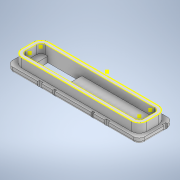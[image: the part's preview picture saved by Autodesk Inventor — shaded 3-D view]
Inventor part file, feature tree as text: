
AUTODESK INVENTOR PART (.ipt)
format: ipt  version: 2022 (Build 260153000, 153)  size: 633,344 bytes
history: native  units: in
note: dims shown in document units (in); Inventor stores cm internally (conversion verified against a paired STEP export)
features: extrude x24, sketch x24, projected_geometry x18, fillet x7, mirror x2, plane x1
ambient origin geometry x8: Origin, YZ Plane, XZ Plane, XY Plane, X Axis, Y Axis, Z Axis, Center Point
bodies: Solid1 (feature_tree)
feature tree (76):
  extrude  "Extrusion1"  Depth=1.875in
  extrude  "Extrusion2"  Depth=0.125in
  fillet  "Fillet1"  Radius=2.0in
  extrude  "Extrusion3"  Depth=0.125in
  fillet  "Fillet2"  Radius=0.4in
  sketch  "Sketch4"  dims[d10=1.0in d11=0.25in d12=0.0in d13=0.125in]
  extrude  "Extrusion4"  Depth=0.125in TaperAngle=0.0deg
  fillet  "Fillet4"  Radius=0.125in
  extrude  "Extrusion6"  Depth=0.125in
  fillet  "Fillet5"  Radius=0.125in
  extrude  "Extrusion7"  Depth=0.0394in TaperAngle=0.0deg
  mirror  "Mirror1"
  extrude  "Extrusion8"  Depth=0.0394in
  fillet  "Fillet6"  Radius=0.0394in
  mirror  "Mirror2"
  sketch  "Sketch7"  dims[d27=0.55in d28=0.0787in d29=0.0394in d30=0.0in]
  plane  "Work Plane1"
  extrude  "Extrusion9"  Depth=0.125in TaperAngle=0.0deg
  extrude  "Extrusion10"  Depth=0.375in
  extrude  "Extrusion11"  Depth=1.0in
  extrude  "Extrusion12"  Depth=0.0625in
  extrude  "Extrusion13"  Depth=0.125in TaperAngle=0.0deg
  extrude  "Extrusion15"  Depth=0.4in
  fillet  "Fillet7"  Radius=0.0415in
  sketch  "Sketch15"  dims[d48=0.0415in d50=0.0415in]
  sketch  "Sketch16"  dims[d51=1.0in d52=0.0in d55=0.06in]
  extrude  "Extrusion16"  Depth=0.0415in
  extrude  "Extrusion17"  Depth=0.06in
  extrude  "Extrusion18"  Depth=0.125in
  sketch  "Sketch19"  dims[d64=0.2in d65=0.0in d66=0.011in d67=30.0in d68=0.0in]
  extrude  "Extrusion20"  Depth=30.0in TaperAngle=0.0deg
  extrude  "Extrusion21"  Depth=0.2in
  fillet  "Fillet8"  Radius=30.0in
  extrude  "Extrusion22"  Depth=0.125in TaperAngle=0.0deg
  extrude  "Extrusion23"  Depth=0.0625in
  extrude  "Extrusion24"  Depth=0.1in
  extrude  "Extrusion25"  Depth=0.2in
  extrude  "Extrusion26"  Depth=0.125in
  sketch  "Sketch25"  dims[d83=0.05in d84=0.125in d85=0.0in d86=0.75in d87=0.125in d88=0.0in d89=0.25in d90=0.0in d91=0.25in d92=0.0in d93=0.5in d94=0.0344in d95=0.5in d96=0.0344in]
  extrude  "Extrusion19"  Depth=0.125in TaperAngle=0.0deg
  sketch  "Sketch1"  dims[d0=2.475in d1=1.875in]
  sketch  "Sketch2"  dims[d2=0.75in d3=0.0in d4=0.125in d5=2.0in d6=0.0in]
  projected_geometry  "Projected Loop1"
  sketch  "Sketch3"  dims[d7=0.125in d8=0.12in d9=0.4in]
  projected_geometry  "Projected Loop2"
  sketch  "Sketch5"  dims[d14=0.125in d15=0.0in d19=0.125in d20=0.125in d21=0.0in]
  projected_geometry  "Projected Loop3"
  projected_geometry  "Projected Loop4"
  sketch  "Sketch6"  dims[d22=0.125in d25=0.0394in d26=0.0in]
  projected_geometry  "Projected Loop5"
  projected_geometry  "Projected Loop6"
  projected_geometry  "Projected Loop7"
  projected_geometry  "Projected Loop8"
  projected_geometry  "Projected Loop9"
  projected_geometry  "Projected Loop10"
  sketch  "Sketch8"  dims[d31=0.125in d32=0.125in d33=0.0in]
  sketch  "Sketch9"  dims[d34=2.5in d35=0.0in d36=0.375in]
  projected_geometry  "Projected Loop11"
  sketch  "Sketch10"  dims[d37=1.25in d38=1.0in]
  sketch  "Sketch11"  dims[d39=0.0625in d40=2.0in]
  projected_geometry  "Projected Loop12"
  sketch  "Sketch12"  dims[d41=0.125in d42=10.0in d43=0.0in]
  sketch  "Sketch14"  dims[d44=10.0in d45=0.0in d46=0.4in d47=0.0415in]
  projected_geometry  "Projected Loop14"
  projected_geometry  "Projected Loop15"
  sketch  "Sketch17"  dims[d56=0.125in d57=0.0in d58=0.125in]
  sketch  "Sketch18"  dims[d59=0.08in d60=30.0in d61=0.5in d62=0.0in d63=0.0in]
  projected_geometry  "Projected Loop16"
  projected_geometry  "Projected Loop17"
  sketch  "Sketch20"  dims[d69=0.125in d70=0.0in d71=0.125in d72=0.0in]
  sketch  "Sketch21"  dims[d73=0.125in d74=0.0in d75=0.0625in]
  sketch  "Sketch22"  dims[d76=0.25in d77=0.1in]
  sketch  "Sketch23"  dims[d78=0.5in d79=0.2in]
  sketch  "Sketch24"  dims[d80=0.125in d81=0.0in d82=0.05in]
  projected_geometry  "Projected Loop18"
  projected_geometry  "Projected Loop19"
